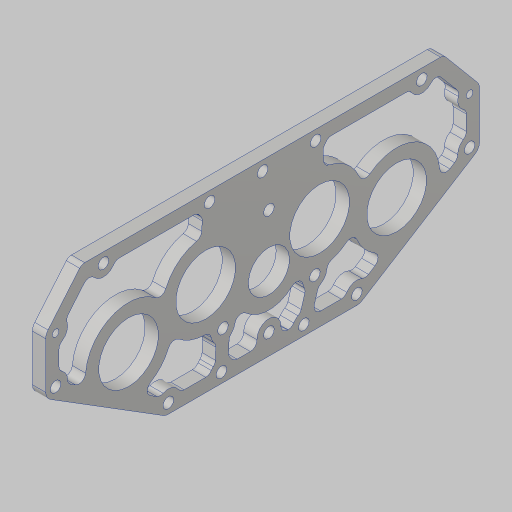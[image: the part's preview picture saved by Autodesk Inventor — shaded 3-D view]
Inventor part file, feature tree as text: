
AUTODESK INVENTOR PART (.ipt)
format: ipt  version: 2023.5 (Build 275446000, 446)  size: 477,184 bytes
history: native  units: in
note: dims shown in document units (in); Inventor stores cm internally (conversion verified against a paired STEP export)
features: sketch x3, hole x3, extrude x2, mirror x2, fillet x1, projected_geometry x1
ambient origin geometry x8: Origin, YZ Plane, XZ Plane, XY Plane, X Axis, Y Axis, Z Axis, Center Point
bodies: Solid1 (feature_tree)
feature tree (12):
  sketch  "Sketch1"  dims[d0=0.125in d1=28.0in]
  sketch  "Sketch3"  dims[d2=2.0in d3=1.0in]
  extrude  "Extrusion1"  Depth=0.125in
  hole  "Mount Holes"  [1 undecoded]
  hole  "Motor Mount"  [1 undecoded]
  mirror  "Mirror1"
  hole  "Hole3"  [1 undecoded]
  mirror  "Mirror2"
  extrude  "Extrusion2"  Depth=0.125in
  fillet  "Fillet2"  Radius=1.0in
  sketch  "Sketch5"  dims[d4=5.5in d5=3.0in d6=1.0in d7=32.0in d8=1.0in d9=0.375in d10=14.0in d11=0.812in d12=0.438in d13=0.3in d23=2.63in d24=2.0in d30=2.256in d31=0.5in d32=2.0in d33=1.0in d34=2.0in d35=0.5in d36=2.0in d37=2.4in d38=1.5in d39=1.375in d40=0.375in d41=1.125in d42=1.125in d43=2.3622in d45=360.0deg d47=2.0in d48=1.0in d49=0.875in d50=0.3in d51=1.0in d52=0.75in d55=0.8933in d57=0.25in d58=0.0in d59=0.201in d60=0.75in d61=0.385in d62=0.25in d63=0.5635in d64=1.0in d65=0.8108in d66=0.775in d68=1.125in d69=1.5in d70=0.201in d71=0.75in d72=0.375in d73=0.25in d74=0.5635in d75=1.0in d76=0.8108in d77=0.13in d78=0.328in d79=0.375in d80=0.25in d81=0.5635in d82=1.0in d83=0.8108in d84=0.25in d85=0.25in d86=0.125in d87=0.125in d88=0.125in d89=0.125in d90=0.125in d91=0.0in d92=0.0in d94=0.125in d95=0.125in d96=0.25in d97=0.125in]
  projected_geometry  "Project Cut Edges1"
note: 3 required parameter values undecoded (feature->parameter linkage not recoverable at this tier; creation-order binding heuristic only, values carry confidence <= 0.55)
